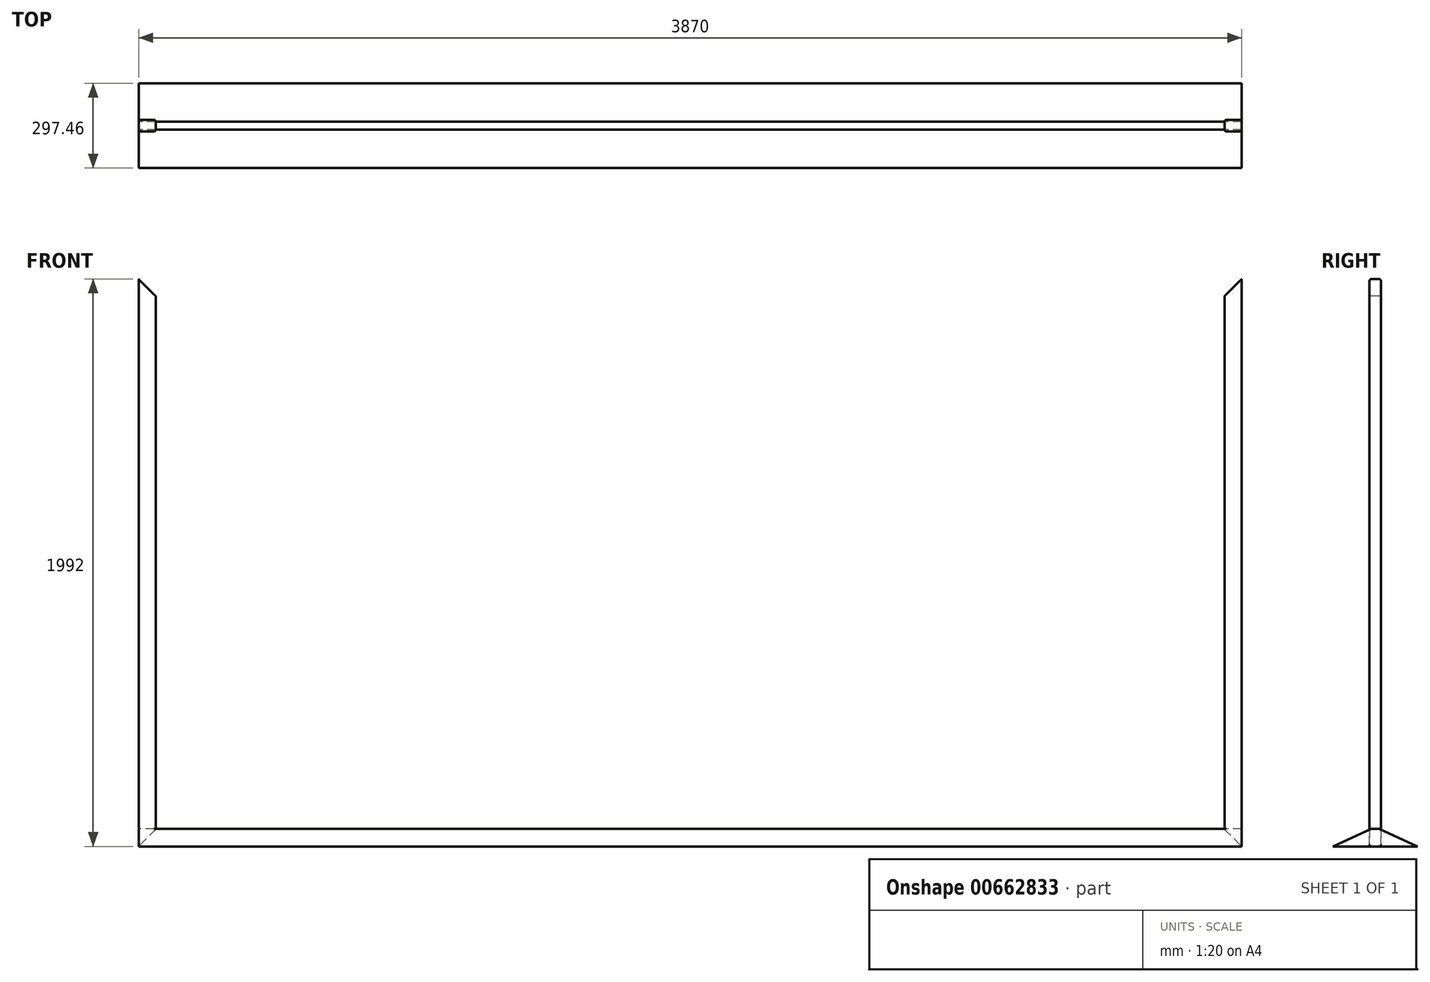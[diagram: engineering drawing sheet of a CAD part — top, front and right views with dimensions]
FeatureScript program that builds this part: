
annotation { "Feature Type Name" : "Feature", "Feature Type Description" : "" }
export const myFeature = defineFeature(function(context is Context, id is Id, definition is map)
    precondition{}
    {
        {
            var Q0;
            Q0=qCreatedBy(makeId("Front.planeOp"),FACE);
            var sketch = newSketch(context, id + "F0", { "sketchPlane" : qUnion([Q0])});
            skLineSegment(sketch, "E0", {"start": v(-1875, 936) * mm, "end": v(-1875, -936) * mm});
            skLineSegment(sketch, "E1", {"start": v(-1935, 996) * mm, "end": v(-1935, -996) * mm});
            skLineSegment(sketch, "E2", {"start": v(-1935, 996) * mm, "end": v(-1875, 936) * mm});
            skLineSegment(sketch, "E3", {"start": v(-1935, -996) * mm, "end": v(-1875, -936) * mm});
            skLineSegment(sketch, "E4.MirrorCS", {"start": v(1935, 996) * mm, "end": v(1875, 936) * mm});
            skLineSegment(sketch, "E5.MirrorCS", {"start": v(1875, 936) * mm, "end": v(1875, -936) * mm});
            skLineSegment(sketch, "E6.MirrorCS", {"start": v(1935, 996) * mm, "end": v(1935, -996) * mm});
            skLineSegment(sketch, "E7.MirrorCS", {"start": v(1935, -996) * mm, "end": v(1875, -936) * mm});
            skSolve(sketch);
        }
        {
            var Q0;
            Q0=makeQuery(id+"F5S7E4SzFwDAVU7_0.imprint","IMPRINT",FACE,{"disambiguationData":[TD([[makeQuery(id+"F5S7E4SzFwDAVU7_0.imprint","IMPRINT",EDGE,{"derivedFrom":sQuery(id+"F5S7E4SzFwDAVU7_0.wireOp",EDGE,"vep6JPTU-KcOV-uCs5-qOqy-pSgM2QAUeQoE")}),-1.0]])]});
            var Q1;
            Q1=makeQuery(id+"F5S7E4SzFwDAVU7_0.imprint","IMPRINT",FACE,{"disambiguationData":[TD([[makeQuery(id+"F5S7E4SzFwDAVU7_0.imprint","IMPRINT",EDGE,{"derivedFrom":sQuery(id+"F5S7E4SzFwDAVU7_0.wireOp",EDGE,"87a2eb86-0931-499b-8b71-f6fbf219887f0.MirrorCS")}),1.0]])]});
            var Q2;
            Q2=makeQuery(id+"F0.imprint","IMPRINT",FACE,{"disambiguationData":[TD([[makeQuery(id+"F0.imprint","IMPRINT",EDGE,{"derivedFrom":sQuery(id+"F0.wireOp",EDGE,"E0")}),-1.0]])]});
            var Q3;
            Q3=makeQuery(id+"F0.imprint","IMPRINT",FACE,{"disambiguationData":[TD([[makeQuery(id+"F0.imprint","IMPRINT",EDGE,{"derivedFrom":sQuery(id+"F0.wireOp",EDGE,"E4.MirrorCS")}),1.0]])]});
            extrude(context, id + "F1", {"entities" : qUnion([Q0, Q1, Q2, Q3]), "endBound" : BoundingType.SYMMETRIC, "oppositeDirection" : true, "depth" : 40 * mm});
        }
        {
            var Q0;
            Q0=qCreatedBy(makeId("Top.planeOp"),FACE);
            var sketch = newSketch(context, id + "F2", { "sketchPlane" : qUnion([Q0])});
            skLineSegment(sketch, "E8.bottom", {"start": v(-761, 17) * mm, "end": v(-809, 17) * mm});
            skLineSegment(sketch, "E8.top", {"start": v(-761, -17) * mm, "end": v(-809, -17) * mm});
            skLineSegment(sketch, "E8.left", {"start": v(-758, 14) * mm, "end": v(-758, -14) * mm});
            skLineSegment(sketch, "E8.right", {"start": v(-812, 14) * mm, "end": v(-812, -14) * mm});
            skPoint(sketch, "E8.middle", {"position": v(-785, 0) * mm});
            skPoint(sketch, "E9.visualSharp", {"position": v(-812, 17) * mm});
            skArc(sketch, "E9.filletArc", {"start": v(-809, 17) * mm, "mid": v(-811.12, 16.12) * mm, "end": v(-812, 14) * mm});
            skPoint(sketch, "E10.visualSharp", {"position": v(-758, 17) * mm});
            skArc(sketch, "E10.filletArc", {"start": v(-758, 14) * mm, "mid": v(-758.88, 16.12) * mm, "end": v(-761, 17) * mm});
            skPoint(sketch, "E11.visualSharp", {"position": v(-758, -17) * mm});
            skArc(sketch, "E11.filletArc", {"start": v(-761, -17) * mm, "mid": v(-758.88, -16.12) * mm, "end": v(-758, -14) * mm});
            skPoint(sketch, "E12.visualSharp", {"position": v(-812, -17) * mm});
            skArc(sketch, "E12.filletArc", {"start": v(-812, -14) * mm, "mid": v(-811.12, -16.12) * mm, "end": v(-809, -17) * mm});
            skArc(sketch, "E13.MirrorCS", {"start": v(812, -14) * mm, "mid": v(811.12, -16.12) * mm, "end": v(809, -17) * mm});
            skArc(sketch, "E14.MirrorCS", {"start": v(809, 17) * mm, "mid": v(811.12, 16.12) * mm, "end": v(812, 14) * mm});
            skLineSegment(sketch, "E15.MirrorCS", {"start": v(812, 14) * mm, "end": v(812, -14) * mm});
            skArc(sketch, "E16.MirrorCS", {"start": v(761, -17) * mm, "mid": v(758.88, -16.12) * mm, "end": v(758, -14) * mm});
            skArc(sketch, "E17.MirrorCS", {"start": v(758, 14) * mm, "mid": v(758.88, 16.12) * mm, "end": v(761, 17) * mm});
            skLineSegment(sketch, "E18.MirrorCS", {"start": v(758, 14) * mm, "end": v(758, -14) * mm});
            skLineSegment(sketch, "E19.MirrorCS", {"start": v(761, 17) * mm, "end": v(809, 17) * mm});
            skLineSegment(sketch, "E20.MirrorCS", {"start": v(761, -17) * mm, "end": v(809, -17) * mm});
            skPoint(sketch, "E21.MirrorP", {"position": v(812, 17) * mm});
            skPoint(sketch, "E22.MirrorP", {"position": v(758, 17) * mm});
            skPoint(sketch, "E23.MirrorP", {"position": v(785, 0) * mm});
            skPoint(sketch, "E24.MirrorP", {"position": v(812, -17) * mm});
            skPoint(sketch, "E25.MirrorP", {"position": v(758, -17) * mm});
            skSolve(sketch);
        }
        {
            var Q0;
            Q0=makeQuery(id+"F2.imprint","IMPRINT",FACE,{"disambiguationData":[TD([[makeQuery(id+"F2.imprint","IMPRINT",EDGE,{"derivedFrom":sQuery(id+"F2.wireOp",EDGE,"E8.bottom")}),1.0]])]});
            var Q1;
            Q1=makeQuery(id+"F2.imprint","IMPRINT",FACE,{"disambiguationData":[TD([[makeQuery(id+"F2.imprint","IMPRINT",EDGE,{"derivedFrom":sQuery(id+"F2.wireOp",EDGE,"E13.MirrorCS")}),-1.0]])]});
            extrude(context, id + "F3", {"entities" : qUnion([Q0, Q1]), "endBound" : BoundingType.SYMMETRIC, "depth" : 955 * mm});
        }
        {
            var Q0;
            Q0=makeQuery(id+"F1.opExtrude","CAP_EDGE",EDGE,{"disambiguationData":[OSD([sQuery(id+"F0.wireOp",EDGE,"E0")])],"isStart":true});
            var Q1;
            Q1=makeQuery(id+"F1.opExtrude","CAP_EDGE",EDGE,{"disambiguationData":[OSD([sQuery(id+"F0.wireOp",EDGE,"E1")])],"isStart":true});
            var Q2;
            Q2=makeQuery(id+"F1.opExtrude","CAP_EDGE",EDGE,{"disambiguationData":[OSD([sQuery(id+"F0.wireOp",EDGE,"E0")])],"isStart":false});
            var Q3;
            Q3=makeQuery(id+"F1.opExtrude","CAP_EDGE",EDGE,{"disambiguationData":[OSD([sQuery(id+"F0.wireOp",EDGE,"E1")])],"isStart":false});
            var Q4;
            Q4=makeQuery(id+"F1.opExtrude","CAP_EDGE",EDGE,{"disambiguationData":[OSD([sQuery(id+"F0.wireOp",EDGE,"E6.MirrorCS")])],"isStart":true});
            var Q5;
            Q5=makeQuery(id+"F1.opExtrude","CAP_EDGE",EDGE,{"disambiguationData":[OSD([sQuery(id+"F0.wireOp",EDGE,"E5.MirrorCS")])],"isStart":true});
            var Q6;
            Q6=makeQuery(id+"F1.opExtrude","CAP_EDGE",EDGE,{"disambiguationData":[OSD([sQuery(id+"F0.wireOp",EDGE,"E6.MirrorCS")])],"isStart":false});
            var Q7;
            Q7=makeQuery(id+"F1.opExtrude","CAP_EDGE",EDGE,{"disambiguationData":[OSD([sQuery(id+"F0.wireOp",EDGE,"E5.MirrorCS")])],"isStart":false});
            fillet(context, id + "F4", {"entities" : qUnion([Q0, Q1, Q2, Q3, Q4, Q5, Q6, Q7]), "radius" : 6 * mm, "tangentPropagation" : true, "allowEdgeOverflow" : false});
        }
        {
            var Q0;
            Q0=makeQuery(id+"F3.opExtrude","SWEPT_BODY",BODY,{"disambiguationData":[OSD([sQuery(id+"F2.wireOp",EDGE,"E8.bottom"),sQuery(id+"F2.wireOp",EDGE,"E8.top"),sQuery(id+"F2.wireOp",EDGE,"E8.left"),sQuery(id+"F2.wireOp",EDGE,"E8.right"),sQuery(id+"F2.wireOp",EDGE,"E9.filletArc"),sQuery(id+"F2.wireOp",EDGE,"E10.filletArc"),sQuery(id+"F2.wireOp",EDGE,"E11.filletArc"),sQuery(id+"F2.wireOp",EDGE,"E12.filletArc")])]});
            var Q1;
            Q1=makeQuery(id+"F3.opExtrude","SWEPT_BODY",BODY,{"disambiguationData":[OSD([sQuery(id+"F2.wireOp",EDGE,"E13.MirrorCS"),sQuery(id+"F2.wireOp",EDGE,"E14.MirrorCS"),sQuery(id+"F2.wireOp",EDGE,"E15.MirrorCS"),sQuery(id+"F2.wireOp",EDGE,"E16.MirrorCS"),sQuery(id+"F2.wireOp",EDGE,"E17.MirrorCS"),sQuery(id+"F2.wireOp",EDGE,"E18.MirrorCS"),sQuery(id+"F2.wireOp",EDGE,"E19.MirrorCS"),sQuery(id+"F2.wireOp",EDGE,"E20.MirrorCS")])]});
            var Q2;
            Q2=makeQuery(id+"F1.opExtrude","SWEPT_BODY",BODY,{"disambiguationData":[OSD([sQuery(id+"F0.wireOp",EDGE,"E4.MirrorCS"),sQuery(id+"F0.wireOp",EDGE,"E5.MirrorCS"),sQuery(id+"F0.wireOp",EDGE,"E6.MirrorCS"),sQuery(id+"F0.wireOp",EDGE,"E7.MirrorCS")])]});
            var Q3;
            Q3=makeQuery(id+"F1.opExtrude","SWEPT_BODY",BODY,{"disambiguationData":[OSD([sQuery(id+"F0.wireOp",EDGE,"E0"),sQuery(id+"F0.wireOp",EDGE,"E1"),sQuery(id+"F0.wireOp",EDGE,"E2"),sQuery(id+"F0.wireOp",EDGE,"E3")])]});
            booleanBodies(context, id + "F5", {"operationType" : BooleanOperationType.SUBTRACTION, "tools" : qUnion([Q0, Q1]), "targets" : qUnion([Q2, Q3])});
        }
        {
            var Q0;
            Q0=qCreatedBy(makeId("Right.planeOp"),FACE);
            var sketch = newSketch(context, id + "F6", { "sketchPlane" : qUnion([Q0])});
            skLineSegment(sketch, "E26", {"start": v(0, -934.35) * mm, "end": v(-14.1, -934.35) * mm});
            skLineSegment(sketch, "E27", {"start": v(0, -996) * mm, "end": v(-148.73, -996) * mm});
            skLineSegment(sketch, "E28", {"start": v(-148.73, -996) * mm, "end": v(-14.1, -934.35) * mm});
            skLineSegment(sketch, "E29.MirrorCS", {"start": v(0, -934.35) * mm, "end": v(14.1, -934.35) * mm});
            skLineSegment(sketch, "E30.MirrorCS", {"start": v(148.73, -996) * mm, "end": v(14.1, -934.35) * mm});
            skLineSegment(sketch, "E31.MirrorCS", {"start": v(0, -996) * mm, "end": v(148.73, -996) * mm});
            skSolve(sketch);
        }
        {
            var Q0;
            Q0 = qSketchRegion(id + "F6", true);
            var Q1;
            Q1=sQuery(id+"F0.wireOp",VERTEX,"E7.MirrorCS.start");
            var Q2;
            Q2=sQuery(id+"F0.wireOp",VERTEX,"E3.start");
            extrude(context, id + "F7", {"entities" : qUnion([Q0]), "endBound" : BoundingType.UP_TO_VERTEX, "depth" : 25 * mm, "endBoundEntityVertex" : qUnion([Q1]), "offsetDistance" : 25 * mm, "hasSecondDirection" : true, "secondDirectionBound" : SecondDirectionBoundingType.UP_TO_VERTEX, "secondDirectionOppositeDirection" : true, "secondDirectionDepth" : 25 * mm, "secondDirectionBoundEntityVertex" : qUnion([Q2])});
        }
        {
            var Q0;
            Q0=makeQuery(id+"F7.opExtrude","SWEPT_FACE",FACE,{"disambiguationData":[OSD([sQuery(id+"F6.wireOp",EDGE,"E28")])]});
            var sketch = newSketch(context, id + "F8", { "sketchPlane" : qUnion([Q0])});
            skLineSegment(sketch, "E32.bottom", {"start": v(-1875.4, -178.12) * mm, "end": v(1874.99, -178.12) * mm});
            skLineSegment(sketch, "E32.top", {"start": v(-1875.4, -173.97) * mm, "end": v(1874.99, -173.97) * mm});
            skLineSegment(sketch, "E32.left", {"start": v(-1875.4, -178.12) * mm, "end": v(-1875.4, -173.97) * mm});
            skLineSegment(sketch, "E32.right", {"start": v(1874.99, -178.12) * mm, "end": v(1874.99, -173.97) * mm});
            skLineSegment(sketch, "E33.MirrorCS", {"start": v(1874.99, -169.82) * mm, "end": v(1874.99, -173.97) * mm});
            skLineSegment(sketch, "E34.MirrorCS", {"start": v(-1875.4, -169.82) * mm, "end": v(1874.99, -169.82) * mm});
            skLineSegment(sketch, "E35.MirrorCS", {"start": v(-1875.4, -169.82) * mm, "end": v(-1875.4, -173.97) * mm});
            skSolve(sketch);
        }
        {
            var Q0;
            Q0 = qSketchRegion(id + "F8", true);
            extrude(context, id + "F9", {"entities" : qUnion([Q0]), "operationType" : NewBodyOperationType.REMOVE, "oppositeDirection" : true, "depth" : 10 * mm, "offsetDistance" : 25 * mm});
        }
    });
